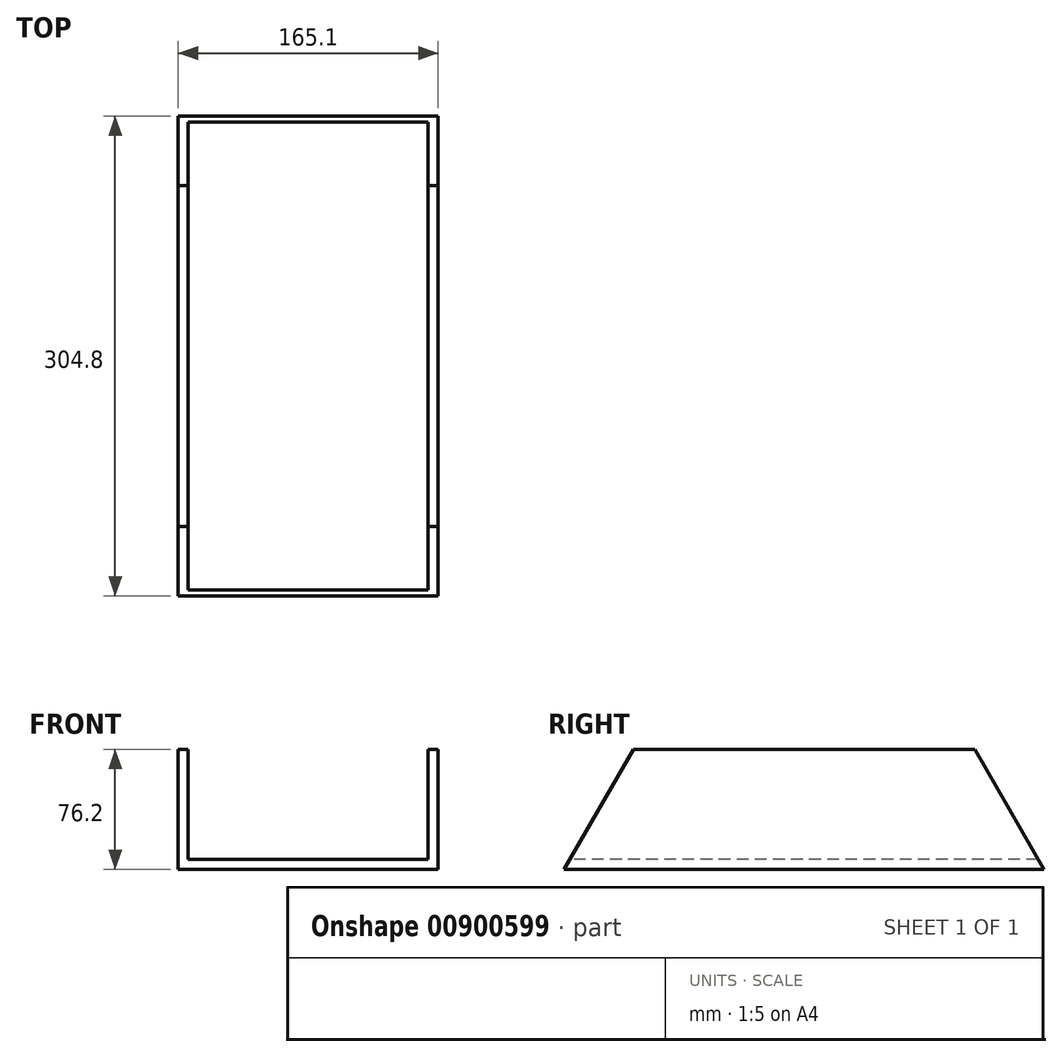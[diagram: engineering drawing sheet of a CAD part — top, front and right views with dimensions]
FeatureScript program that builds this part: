
annotation { "Feature Type Name" : "Feature", "Feature Type Description" : "" }
export const myFeature = defineFeature(function(context is Context, id is Id, definition is map)
    precondition{}
    {
        {
            var Q0;
            Q0=qCreatedBy(makeId("Right.planeOp"),FACE);
            var sketch = newSketch(context, id + "F0", { "sketchPlane" : qUnion([Q0])});
            skLineSegment(sketch, "E0", {"start": v(0, 0) * mm, "end": v(203.2, 0) * mm});
            skLineSegment(sketch, "E1", {"start": v(199.53, 6.35) * mm, "end": v(0, 6.35) * mm});
            skLineSegment(sketch, "E2", {"start": v(0, 6.35) * mm, "end": v(0, 0) * mm});
            skLineSegment(sketch, "E3", {"start": v(203.2, 0) * mm, "end": v(199.53, 6.35) * mm});
            skPoint(sketch, "E4.end.orphan", {"position": v(203.2, 25.25) * mm});
            skPoint(sketch, "E5.end.orphan", {"position": v(203.2, 6.35) * mm});
            skSolve(sketch);
        }
        {
            var Q0;
            Q0 = qSketchRegion(id + "F0", true);
            extrude(context, id + "F1", {"entities" : qUnion([Q0]), "depth" : 152.4 * mm, "offsetDistance" : 25.4 * mm});
        }
        {
            var Q0;
            Q0=makeQuery(id+"F1.opExtrude","CAP_FACE",FACE,{"disambiguationData":[OSD([sQuery(id+"F0.wireOp",EDGE,"E0"),sQuery(id+"F0.wireOp",EDGE,"E1"),sQuery(id+"F0.wireOp",EDGE,"E2"),sQuery(id+"F0.wireOp",EDGE,"E3")])],"isStart":false});
            var sketch = newSketch(context, id + "F2", { "sketchPlane" : qUnion([Q0])});
            skLineSegment(sketch, "E6", {"start": v(203.2, 0) * mm, "end": v(159.2, 76.2) * mm});
            skLineSegment(sketch, "E7", {"start": v(159.2, 76.2) * mm, "end": v(0, 76.2) * mm});
            skLineSegment(sketch, "E8", {"start": v(0, 76.2) * mm, "end": v(0, 0) * mm});
            skLineSegment(sketch, "E9", {"start": v(0, 0) * mm, "end": v(203.2, 0) * mm});
            skSolve(sketch);
        }
        {
            var Q0;
            Q0 = qSketchRegion(id + "F2", true);
            extrude(context, id + "F3", {"entities" : qUnion([Q0]), "operationType" : NewBodyOperationType.ADD, "depth" : 6.35 * mm, "offsetDistance" : 25.4 * mm});
        }
        {
            var Q0;
            Q0=makeQuery(id+"F1.opExtrude","CAP_FACE",FACE,{"disambiguationData":[OSD([sQuery(id+"F0.wireOp",EDGE,"E0"),sQuery(id+"F0.wireOp",EDGE,"E1"),sQuery(id+"F0.wireOp",EDGE,"E2"),sQuery(id+"F0.wireOp",EDGE,"E3")])],"isStart":true});
            var sketch = newSketch(context, id + "F4", { "sketchPlane" : qUnion([Q0])});
            skLineSegment(sketch, "E10", {"start": v(-203.2, 0) * mm, "end": v(-159.2, 76.2) * mm});
            skLineSegment(sketch, "E11", {"start": v(-159.2, 76.2) * mm, "end": v(0, 76.2) * mm});
            skLineSegment(sketch, "E12", {"start": v(0, 76.2) * mm, "end": v(0, 0) * mm});
            skLineSegment(sketch, "E13", {"start": v(0, 0) * mm, "end": v(-203.2, 0) * mm});
            skSolve(sketch);
        }
        {
            var Q0;
            Q0 = qSketchRegion(id + "F4", true);
            extrude(context, id + "F5", {"entities" : qUnion([Q0]), "operationType" : NewBodyOperationType.ADD, "depth" : 6.35 * mm, "offsetDistance" : 25.4 * mm});
        }
        {
            var Q0;
            Q0=makeQuery(id+"F5.boolean.opBoolean","MERGE",FACE,{"derivedFrom":[makeQuery(id+"F3.boolean.opBoolean","MERGE",FACE,{"derivedFrom":[makeQuery(id+"F1.opExtrude","SWEPT_FACE",FACE,{"disambiguationData":[OSD([sQuery(id+"F0.wireOp",EDGE,"E2")])]}),makeQuery(id+"F3.opExtrude","SWEPT_FACE",FACE,{"disambiguationData":[OSD([sQuery(id+"F2.wireOp",EDGE,"E8")])]})]}),makeQuery(id+"F5.opExtrude","SWEPT_FACE",FACE,{"disambiguationData":[OSD([sQuery(id+"F4.wireOp",EDGE,"E12")])]})]});
            var sketch = newSketch(context, id + "F6", { "sketchPlane" : qUnion([Q0])});
            skSolve(sketch);
        }
        {
            var Q0;
            {var subQ0=sQuery(id+"F2.wireOp",EDGE,"E8");Q0=makeQuery(id+"F6.imprint","IMPRINT",FACE,{"disambiguationData":[TD([[makeQuery(id+"F6.imprint","IMPRINT",EDGE,{"derivedFrom":makeQuery(id+"F3.opExtrude","CAP_EDGE",EDGE,{"disambiguationData":[OSD([subQ0])],"isStart":false})}),-1.0]])]});}
            extrude(context, id + "F7", {"entities" : qUnion([Q0]), "operationType" : NewBodyOperationType.ADD, "depth" : 101.6 * mm, "offsetDistance" : 25.4 * mm});
        }
        {
            var Q0;
            {var subQ0=sQuery(id+"F4.wireOp",EDGE,"E12");Q0=makeQuery(id+"F7.boolean.opBoolean","MERGE",FACE,{"derivedFrom":[makeQuery(id+"F5.opExtrude","CAP_FACE",FACE,{"disambiguationData":[OSD([sQuery(id+"F4.wireOp",EDGE,"E10"),sQuery(id+"F4.wireOp",EDGE,"E11"),subQ0,sQuery(id+"F4.wireOp",EDGE,"E13")])],"isStart":false}),makeQuery(id+"F7.opExtrude","SWEPT_FACE",FACE,{"disambiguationData":[OSD([subQ0]),TDD([makeQuery(id+"F6.imprint","IMPRINT",EDGE,{"derivedFrom":makeQuery(id+"F5.opExtrude","CAP_EDGE",EDGE,{"disambiguationData":[OSD([subQ0])],"isStart":false})})])]})]});}
            var sketch = newSketch(context, id + "F8", { "sketchPlane" : qUnion([Q0])});
            skLineSegment(sketch, "E14", {"start": v(101.6, 0) * mm, "end": v(57.6, 76.2) * mm});
            skLineSegment(sketch, "E15", {"start": v(57.6, 76.2) * mm, "end": v(101.6, 76.2) * mm});
            skLineSegment(sketch, "E16", {"start": v(101.6, 76.2) * mm, "end": v(101.6, 0) * mm});
            skSolve(sketch);
        }
        {
            var Q0;
            Q0 = qSketchRegion(id + "F8", true);
            extrude(context, id + "F9", {"entities" : qUnion([Q0]), "operationType" : NewBodyOperationType.REMOVE, "oppositeDirection" : true, "depth" : 165.1 * mm, "offsetDistance" : 25.4 * mm});
        }
    });
